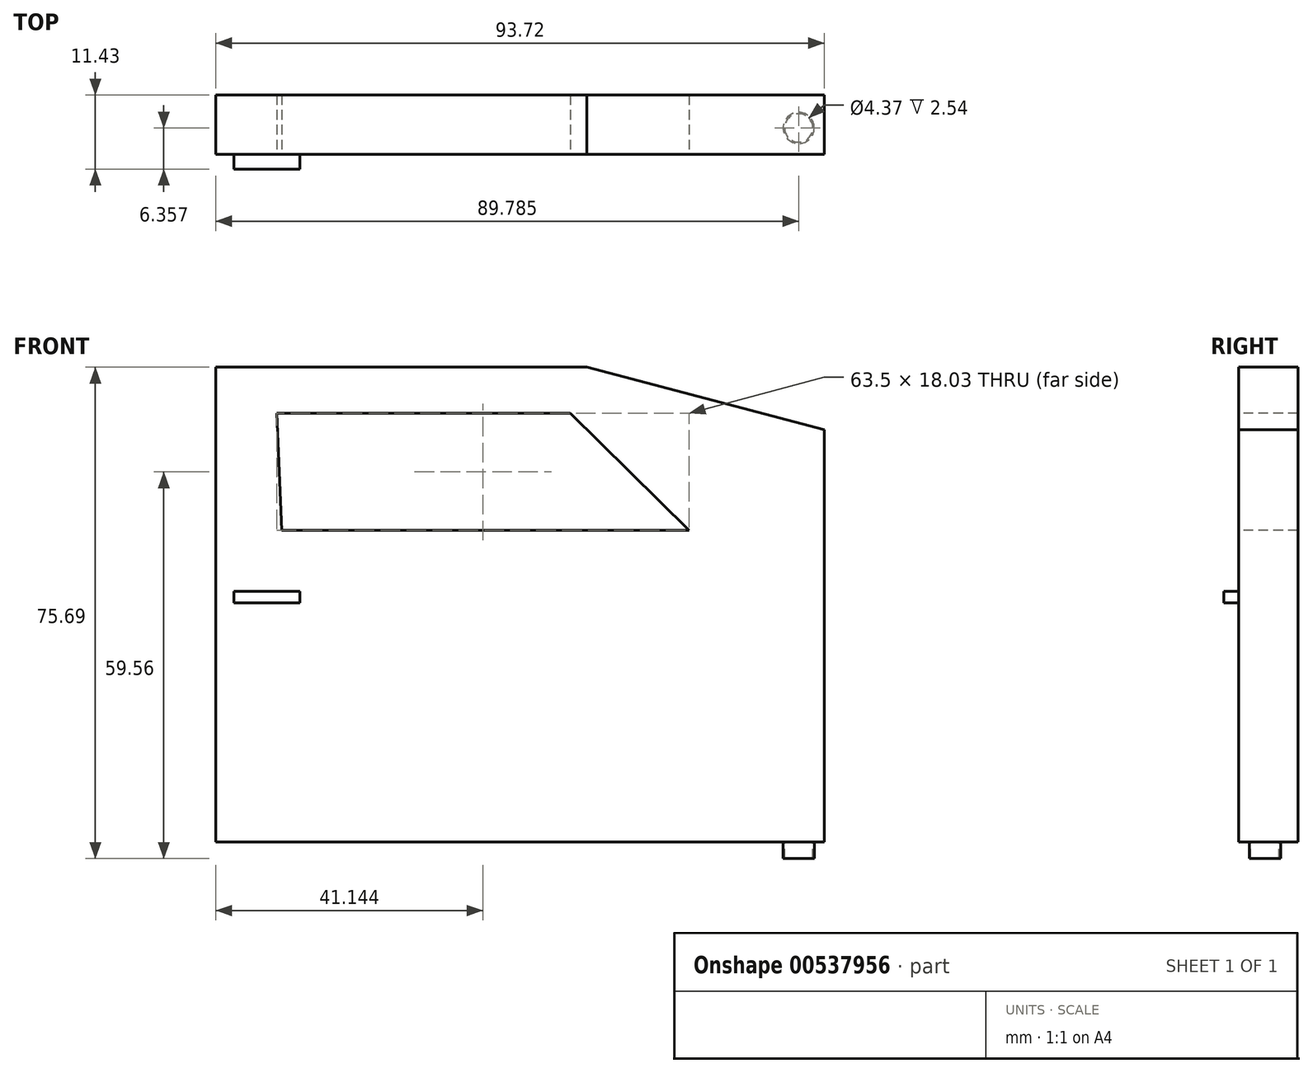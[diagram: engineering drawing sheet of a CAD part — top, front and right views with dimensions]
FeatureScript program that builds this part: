
annotation { "Feature Type Name" : "Feature", "Feature Type Description" : "" }
export const myFeature = defineFeature(function(context is Context, id is Id, definition is map)
    precondition{}
    {
        {
            var Q0;
            Q0=qCreatedBy(makeId("Front.planeOp"),FACE);
            var sketch = newSketch(context, id + "F0", { "sketchPlane" : qUnion([Q0])});
            skLineSegment(sketch, "E0.bottom", {"start": v(-45.97, 31.24) * mm, "end": v(47.75, 31.24) * mm});
            skLineSegment(sketch, "E0.top", {"start": v(-45.97, -41.91) * mm, "end": v(47.75, -41.91) * mm});
            skLineSegment(sketch, "E0.left", {"start": v(-45.97, 31.24) * mm, "end": v(-45.97, -41.91) * mm});
            skLineSegment(sketch, "E0.right", {"start": v(47.75, 31.24) * mm, "end": v(47.75, -41.91) * mm});
            skSolve(sketch);
        }
        {
            var Q0;
            Q0=makeQuery(id+"F0.imprint","IMPRINT",FACE,{"disambiguationData":[TD([[makeQuery(id+"F0.imprint","IMPRINT",EDGE,{"derivedFrom":sQuery(id+"F0.wireOp",EDGE,"E0.bottom")}),-1.0]])]});
            extrude(context, id + "F1", {"entities" : qUnion([Q0]), "depth" : 10.16 * mm, "offsetDistance" : 25.4 * mm});
        }
        {
            var Q0;
            Q0=makeQuery(id+"F1.opExtrude","CAP_FACE",FACE,{"disambiguationData":[OSD([sQuery(id+"F0.wireOp",EDGE,"E0.bottom"),sQuery(id+"F0.wireOp",EDGE,"E0.top"),sQuery(id+"F0.wireOp",EDGE,"E0.left"),sQuery(id+"F0.wireOp",EDGE,"E0.right")])],"isStart":false});
            var sketch = newSketch(context, id + "F2", { "sketchPlane" : qUnion([Q0])});
            skLineSegment(sketch, "E1", {"start": v(11.18, 31.24) * mm, "end": v(47.75, 21.59) * mm});
            skLineSegment(sketch, "E2", {"start": v(47.75, 31.24) * mm, "end": v(11.18, 31.24) * mm});
            skLineSegment(sketch, "E3", {"start": v(47.75, 21.59) * mm, "end": v(47.75, 31.24) * mm});
            skSolve(sketch);
        }
        {
            var Q0;
            Q0 = qSketchRegion(id + "F2", true);
            extrude(context, id + "F3", {"entities" : qUnion([Q0]), "operationType" : NewBodyOperationType.REMOVE, "oppositeDirection" : true, "depth" : 10.16 * mm, "offsetDistance" : 25.4 * mm});
        }
        {
            var Q0;
            Q0=makeQuery(id+"F1.opExtrude","CAP_FACE",FACE,{"disambiguationData":[OSD([sQuery(id+"F0.wireOp",EDGE,"E0.bottom"),sQuery(id+"F0.wireOp",EDGE,"E0.top"),sQuery(id+"F0.wireOp",EDGE,"E0.left"),sQuery(id+"F0.wireOp",EDGE,"E0.right")])],"isStart":false});
            var sketch = newSketch(context, id + "F4", { "sketchPlane" : qUnion([Q0])});
            skLineSegment(sketch, "E4", {"start": v(-36.58, 24.13) * mm, "end": v(8.64, 24.13) * mm});
            skLineSegment(sketch, "E5", {"start": v(8.64, 24.13) * mm, "end": v(26.92, 6.1) * mm});
            skLineSegment(sketch, "E6", {"start": v(26.92, 6.1) * mm, "end": v(-35.81, 6.1) * mm});
            skLineSegment(sketch, "E7", {"start": v(-35.81, 6.1) * mm, "end": v(-36.58, 24.13) * mm});
            skSolve(sketch);
        }
        {
            var Q0;
            Q0 = qSketchRegion(id + "F4", true);
            extrude(context, id + "F5", {"entities" : qUnion([Q0]), "operationType" : NewBodyOperationType.REMOVE, "oppositeDirection" : true, "depth" : 10.16 * mm, "offsetDistance" : 25.4 * mm});
        }
        {
            var Q0;
            Q0=makeQuery(id+"F1.opExtrude","CAP_FACE",FACE,{"disambiguationData":[OSD([sQuery(id+"F0.wireOp",EDGE,"E0.bottom"),sQuery(id+"F0.wireOp",EDGE,"E0.top"),sQuery(id+"F0.wireOp",EDGE,"E0.left"),sQuery(id+"F0.wireOp",EDGE,"E0.right")])],"isStart":false});
            extrude(context, id + "F6", {"entities" : qUnion([Q0]), "operationType" : NewBodyOperationType.ADD, "depth" : 25.4 * mm, "offsetDistance" : 25.4 * mm});
        }
        {
            var Q0;
            Q0=makeQuery(id+"F6.opExtrude","CAP_FACE",FACE,{"disambiguationData":[OSD([sQuery(id+"F0.wireOp",EDGE,"E0.bottom"),sQuery(id+"F0.wireOp",EDGE,"E0.top"),sQuery(id+"F0.wireOp",EDGE,"E0.left"),sQuery(id+"F0.wireOp",EDGE,"E0.right")])],"isStart":false});
            var sketch = newSketch(context, id + "F7", { "sketchPlane" : qUnion([Q0])});
            skLineSegment(sketch, "E8.bottom", {"start": v(-43.18, -3.3) * mm, "end": v(-33.02, -3.3) * mm});
            skLineSegment(sketch, "E8.top", {"start": v(-43.18, -5.08) * mm, "end": v(-33.02, -5.08) * mm});
            skLineSegment(sketch, "E8.left", {"start": v(-43.18, -3.3) * mm, "end": v(-43.18, -5.08) * mm});
            skLineSegment(sketch, "E8.right", {"start": v(-33.02, -3.3) * mm, "end": v(-33.02, -5.08) * mm});
            skSolve(sketch);
        }
        {
            var Q0;
            Q0=makeQuery(id+"F7.imprint","IMPRINT",FACE,{"disambiguationData":[TD([[makeQuery(id+"F7.imprint","IMPRINT",EDGE,{"derivedFrom":sQuery(id+"F7.wireOp",EDGE,"E8.bottom")}),-1.0]])]});
            extrude(context, id + "F8", {"entities" : qUnion([Q0]), "operationType" : NewBodyOperationType.ADD, "depth" : 2.3 * mm, "offsetDistance" : 25.4 * mm});
        }
        {
            var Q0;
            {var subQ0=sQuery(id+"F0.wireOp",EDGE,"E0.left");Q0=makeQuery(id+"F6.boolean.opBoolean","MERGE",FACE,{"derivedFrom":[makeQuery(id+"F1.opExtrude","SWEPT_FACE",FACE,{"disambiguationData":[OSD([subQ0])]}),makeQuery(id+"F6.opExtrude","SWEPT_FACE",FACE,{"disambiguationData":[OSD([subQ0])]})]});}
            var sketch = newSketch(context, id + "F9", { "sketchPlane" : qUnion([Q0])});
            skLineSegment(sketch, "E9.bottom", {"start": v(0, 31.24) * mm, "end": v(26.42, 31.24) * mm});
            skLineSegment(sketch, "E9.top", {"start": v(0, -41.91) * mm, "end": v(26.42, -41.91) * mm});
            skLineSegment(sketch, "E9.left", {"start": v(0, 31.24) * mm, "end": v(0, -41.91) * mm});
            skLineSegment(sketch, "E9.right", {"start": v(26.42, 31.24) * mm, "end": v(26.42, -41.91) * mm});
            skSolve(sketch);
        }
        {
            var Q0;
            Q0 = qSketchRegion(id + "F9", true);
            extrude(context, id + "F10", {"entities" : qUnion([Q0]), "operationType" : NewBodyOperationType.REMOVE, "oppositeDirection" : true, "depth" : 127 * mm, "offsetDistance" : 25.4 * mm});
        }
        {
            var Q0;
            {var subQ0=sQuery(id+"F0.wireOp",EDGE,"E0.top");Q0=makeQuery(id+"F6.boolean.opBoolean","MERGE",FACE,{"derivedFrom":[makeQuery(id+"F1.opExtrude","SWEPT_FACE",FACE,{"disambiguationData":[OSD([subQ0])]}),makeQuery(id+"F6.opExtrude","SWEPT_FACE",FACE,{"disambiguationData":[OSD([subQ0])]})]});}
            var sketch = newSketch(context, id + "F11", { "sketchPlane" : qUnion([Q0])});
            skCircle(sketch, "E10", {"center": v(-42.3, 31.5) * mm, "radius": 1.98 * mm});
            skSolve(sketch);
        }
        {
            var Q0;
            Q0=makeQuery(id+"F11.imprint","IMPRINT",FACE,{"disambiguationData":[TD([[makeQuery(id+"F11.imprint","IMPRINT",EDGE,{"derivedFrom":sQuery(id+"F11.wireOp",EDGE,"E10")}),-1.0]])]});
            var sketch = newSketch(context, id + "F12", { "sketchPlane" : qUnion([Q0])});
            skCircle(sketch, "E11", {"center": v(43.81, 31.5) * mm, "radius": 2.18 * mm});
            skCircle(sketch, "E12", {"center": v(43.81, 31.5) * mm, "radius": 2.4 * mm});
            skSolve(sketch);
        }
        {
            var Q0;
            Q0 = qSketchRegion(id + "F12", true);
            extrude(context, id + "F13", {"entities" : qUnion([Q0]), "operationType" : NewBodyOperationType.ADD, "depth" : 2.54 * mm, "offsetDistance" : 25.4 * mm});
        }
    });
